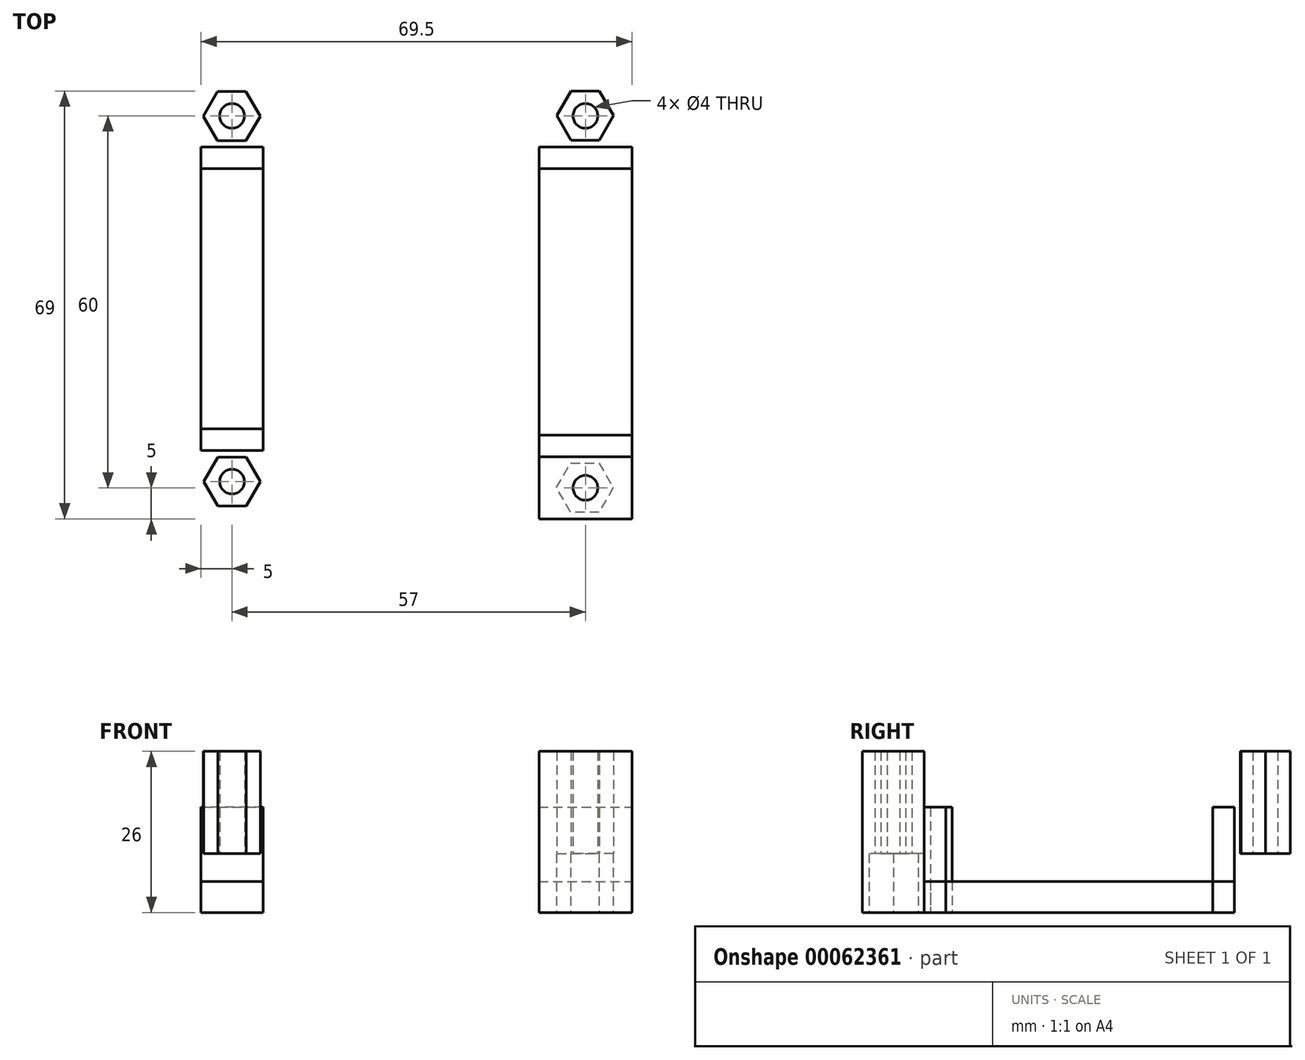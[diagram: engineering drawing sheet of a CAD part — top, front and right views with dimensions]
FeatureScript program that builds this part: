
annotation { "Feature Type Name" : "Feature", "Feature Type Description" : "" }
export const myFeature = defineFeature(function(context is Context, id is Id, definition is map)
    precondition{}
    {
        {
            var Q0;
            Q0=qCreatedBy(makeId("Top.planeOp"),FACE);
            var sketch = newSketch(context, id + "F0", { "sketchPlane" : qUnion([Q0])});
            skLineSegment(sketch, "E0.bottom", {"start": v(0, 0) * mm, "end": v(50.5, 0) * mm, "construction": true});
            skLineSegment(sketch, "E0.top", {"start": v(0, -69) * mm, "end": v(50.5, -69) * mm, "construction": true});
            skLineSegment(sketch, "E0.left", {"start": v(0, 0) * mm, "end": v(0, -69) * mm, "construction": true});
            skLineSegment(sketch, "E0.right", {"start": v(50.5, 0) * mm, "end": v(50.5, -69) * mm, "construction": true});
            skPoint(sketch, "E1", {"position": v(15, 8) * mm});
            skPoint(sketch, "E2", {"position": v(35.5, 8) * mm});
            skPoint(sketch, "E3", {"position": v(35.5, -32) * mm});
            skPoint(sketch, "E4", {"position": v(15, -32) * mm});
            skCircle(sketch, "E5", {"center": v(15, 8) * mm, "radius": 2 * mm});
            skCircle(sketch, "E6", {"center": v(35.5, 8) * mm, "radius": 2 * mm});
            skCircle(sketch, "E7", {"center": v(35.5, -32) * mm, "radius": 2 * mm});
            skCircle(sketch, "E8", {"center": v(15, -32) * mm, "radius": 2 * mm});
            skPoint(sketch, "E9", {"position": v(-9.5, 0) * mm});
            skPoint(sketch, "E10", {"position": v(60, 0) * mm});
            skPoint(sketch, "E11", {"position": v(45, 0) * mm});
            skPoint(sketch, "E12", {"position": v(0.5, 0) * mm});
            skPoint(sketch, "E13", {"position": v(60, -70) * mm});
            skPoint(sketch, "E14", {"position": v(-9.5, -69) * mm});
            skPoint(sketch, "E15", {"position": v(-9.5, -13.5) * mm});
            skPoint(sketch, "E16", {"position": v(-9.5, -55.5) * mm});
            skPoint(sketch, "E17", {"position": v(60, -13.5) * mm});
            skPoint(sketch, "E18", {"position": v(60, -56.5) * mm});
            skLineSegment(sketch, "E19.bottom", {"start": v(45, 0) * mm, "end": v(60, 0) * mm});
            skLineSegment(sketch, "E19.top", {"start": v(45, -70) * mm, "end": v(60, -70) * mm});
            skLineSegment(sketch, "E19.left", {"start": v(45, 0) * mm, "end": v(45, -70) * mm});
            skLineSegment(sketch, "E19.right", {"start": v(60, 0) * mm, "end": v(60, -70) * mm});
            skLineSegment(sketch, "E20.bottom", {"start": v(60, -13.5) * mm, "end": v(45, -13.5) * mm});
            skLineSegment(sketch, "E20.top", {"start": v(60, 0) * mm, "end": v(45, 0) * mm});
            skLineSegment(sketch, "E20.left", {"start": v(60, -13.5) * mm, "end": v(60, 0) * mm});
            skLineSegment(sketch, "E20.right", {"start": v(45, -13.5) * mm, "end": v(45, 0) * mm});
            skLineSegment(sketch, "E21.top", {"start": v(45, -56.5) * mm, "end": v(60, -56.5) * mm});
            skLineSegment(sketch, "E21.left", {"start": v(45, -70) * mm, "end": v(45, -56.5) * mm});
            skLineSegment(sketch, "E21.right", {"start": v(60, -70) * mm, "end": v(60, -56.5) * mm});
            skLineSegment(sketch, "E22.bottom", {"start": v(-9.5, -69) * mm, "end": v(0.5, -69) * mm});
            skLineSegment(sketch, "E22.top", {"start": v(-9.5, 0) * mm, "end": v(0.5, 0) * mm});
            skLineSegment(sketch, "E22.left", {"start": v(-9.5, -69) * mm, "end": v(-9.5, 0) * mm});
            skLineSegment(sketch, "E22.right", {"start": v(0.5, -69) * mm, "end": v(0.5, 0) * mm});
            skLineSegment(sketch, "E23.bottom", {"start": v(0.5, 0) * mm, "end": v(-9.5, 0) * mm});
            skLineSegment(sketch, "E23.top", {"start": v(0.5, -13.5) * mm, "end": v(-9.5, -13.5) * mm});
            skLineSegment(sketch, "E23.left", {"start": v(0.5, 0) * mm, "end": v(0.5, -13.5) * mm});
            skLineSegment(sketch, "E23.right", {"start": v(-9.5, 0) * mm, "end": v(-9.5, -13.5) * mm});
            skLineSegment(sketch, "E24.bottom", {"start": v(0.5, -69) * mm, "end": v(-9.5, -69) * mm});
            skLineSegment(sketch, "E24.top", {"start": v(0.5, -55.5) * mm, "end": v(-9.5, -55.5) * mm});
            skLineSegment(sketch, "E24.left", {"start": v(0.5, -69) * mm, "end": v(0.5, -55.5) * mm});
            skLineSegment(sketch, "E24.right", {"start": v(-9.5, -69) * mm, "end": v(-9.5, -55.5) * mm});
            skLineSegment(sketch, "E25", {"start": v(-9.5, -10) * mm, "end": v(0.5, -10) * mm});
            skLineSegment(sketch, "E26", {"start": v(-9.5, -59) * mm, "end": v(0.5, -59) * mm});
            skLineSegment(sketch, "E27", {"start": v(45, -60) * mm, "end": v(60, -60) * mm});
            skLineSegment(sketch, "E28", {"start": v(45, -10) * mm, "end": v(60, -10) * mm});
            skCircle(sketch, "E29", {"center": v(-4.5, -5) * mm, "radius": 2 * mm});
            skPoint(sketch, "E29.centerSnap0", {"position": v(-4.5, 0) * mm});
            skCircle(sketch, "E30", {"center": v(52.5, -5) * mm, "radius": 2 * mm});
            skPoint(sketch, "E30.centerSnap0", {"position": v(52.5, 0) * mm});
            skCircle(sketch, "E31", {"center": v(52.5, -65) * mm, "radius": 2 * mm});
            skPoint(sketch, "E31.centerSnap0", {"position": v(52.5, -70) * mm});
            skCircle(sketch, "E32", {"center": v(-4.5, -64) * mm, "radius": 2 * mm});
            skPoint(sketch, "E32.centerSnap0", {"position": v(-4.5, -69) * mm});
            skPoint(sketch, "E33", {"position": v(15, 16) * mm});
            skPoint(sketch, "E34", {"position": v(35.53, 16) * mm});
            skPoint(sketch, "E35", {"position": v(7, 8) * mm});
            skPoint(sketch, "E36", {"position": v(43.5, 8) * mm});
            skLineSegment(sketch, "E37", {"start": v(15, 16) * mm, "end": v(35.53, 16) * mm});
            skLineSegment(sketch, "E38", {"start": v(43.5, 8) * mm, "end": v(35.53, 16) * mm});
            skLineSegment(sketch, "E39", {"start": v(7, 8) * mm, "end": v(15, 16) * mm});
            skLineSegment(sketch, "E40", {"start": v(43.5, 8) * mm, "end": v(45, -10) * mm});
            skLineSegment(sketch, "E41", {"start": v(7, 8) * mm, "end": v(0.5, -10) * mm});
            skLineSegment(sketch, "E42", {"start": v(0.5, -59) * mm, "end": v(45, -60) * mm});
            skLineSegment(sketch, "E43", {"start": v(-58.4, 29.71) * mm, "end": v(-57.23, 30.88) * mm});
            skLineSegment(sketch, "E44", {"start": v(-57.23, 30.88) * mm, "end": v(-55.57, 30.88) * mm});
            skLineSegment(sketch, "E45", {"start": v(-55.57, 30.88) * mm, "end": v(-54.4, 29.71) * mm});
            skLineSegment(sketch, "E46", {"start": v(-54.4, 29.71) * mm, "end": v(-54.4, 28.05) * mm});
            skLineSegment(sketch, "E47", {"start": v(-54.4, 28.05) * mm, "end": v(-55.57, 26.88) * mm});
            skLineSegment(sketch, "E48", {"start": v(-55.57, 26.88) * mm, "end": v(-57.2, 26.88) * mm});
            skLineSegment(sketch, "E49", {"start": v(-57.2, 26.88) * mm, "end": v(-58.4, 28.03) * mm});
            skLineSegment(sketch, "E50", {"start": v(-58.4, 28.03) * mm, "end": v(-58.4, 29.71) * mm});
            skLineSegment(sketch, "E51.4", {"start": v(-64.18, 24.73) * mm, "end": v(-61.28, 24.73) * mm});
            skLineSegment(sketch, "E51.5", {"start": v(-61.28, 24.73) * mm, "end": v(-59.23, 22.67) * mm});
            skLineSegment(sketch, "E51.6", {"start": v(-59.23, 22.67) * mm, "end": v(-59.23, 19.78) * mm});
            skLineSegment(sketch, "E51.7", {"start": v(-59.23, 19.78) * mm, "end": v(-61.28, 17.73) * mm});
            skLineSegment(sketch, "E51.3", {"start": v(-61.28, 17.73) * mm, "end": v(-64.13, 17.73) * mm});
            skLineSegment(sketch, "E51.1", {"start": v(-64.13, 17.73) * mm, "end": v(-66.23, 19.73) * mm});
            skLineSegment(sketch, "E51.0", {"start": v(-66.23, 19.73) * mm, "end": v(-66.23, 22.67) * mm});
            skLineSegment(sketch, "E51.2", {"start": v(-66.23, 22.67) * mm, "end": v(-64.18, 24.73) * mm});
            skLineSegment(sketch, "E52.4", {"start": v(13.56, 11.51) * mm, "end": v(16.46, 11.51) * mm});
            skLineSegment(sketch, "E52.5", {"start": v(16.46, 11.51) * mm, "end": v(18.51, 9.46) * mm});
            skLineSegment(sketch, "E52.6", {"start": v(18.51, 9.46) * mm, "end": v(18.51, 6.56) * mm});
            skLineSegment(sketch, "E52.7", {"start": v(18.51, 6.56) * mm, "end": v(16.46, 4.51) * mm});
            skLineSegment(sketch, "E52.3", {"start": v(16.46, 4.51) * mm, "end": v(13.61, 4.51) * mm});
            skLineSegment(sketch, "E52.1", {"start": v(13.61, 4.51) * mm, "end": v(11.51, 6.51) * mm});
            skLineSegment(sketch, "E52.0", {"start": v(11.51, 6.51) * mm, "end": v(11.51, 9.46) * mm});
            skLineSegment(sketch, "E52.2", {"start": v(11.51, 9.46) * mm, "end": v(13.56, 11.51) * mm});
            skLineSegment(sketch, "E53.4", {"start": v(34.08, 11.49) * mm, "end": v(36.98, 11.49) * mm});
            skLineSegment(sketch, "E53.5", {"start": v(36.98, 11.49) * mm, "end": v(39.03, 9.44) * mm});
            skLineSegment(sketch, "E53.6", {"start": v(39.03, 9.44) * mm, "end": v(39.03, 6.54) * mm});
            skLineSegment(sketch, "E53.7", {"start": v(39.03, 6.54) * mm, "end": v(36.98, 4.5) * mm});
            skLineSegment(sketch, "E53.3", {"start": v(36.98, 4.5) * mm, "end": v(34.13, 4.5) * mm});
            skLineSegment(sketch, "E53.1", {"start": v(34.13, 4.5) * mm, "end": v(32.03, 6.5) * mm});
            skLineSegment(sketch, "E53.0", {"start": v(32.03, 6.5) * mm, "end": v(32.03, 9.44) * mm});
            skLineSegment(sketch, "E53.2", {"start": v(32.03, 9.44) * mm, "end": v(34.08, 11.49) * mm});
            skLineSegment(sketch, "E54.4", {"start": v(13.56, -28.5) * mm, "end": v(16.46, -28.5) * mm});
            skLineSegment(sketch, "E54.5", {"start": v(16.46, -28.5) * mm, "end": v(18.51, -30.56) * mm});
            skLineSegment(sketch, "E54.6", {"start": v(18.51, -30.56) * mm, "end": v(18.51, -33.46) * mm});
            skLineSegment(sketch, "E54.7", {"start": v(18.51, -33.46) * mm, "end": v(16.46, -35.5) * mm});
            skLineSegment(sketch, "E54.3", {"start": v(16.46, -35.5) * mm, "end": v(13.61, -35.5) * mm});
            skLineSegment(sketch, "E54.1", {"start": v(13.61, -35.5) * mm, "end": v(11.51, -33.5) * mm});
            skLineSegment(sketch, "E54.0", {"start": v(11.51, -33.5) * mm, "end": v(11.51, -30.56) * mm});
            skLineSegment(sketch, "E54.2", {"start": v(11.51, -30.56) * mm, "end": v(13.56, -28.5) * mm});
            skLineSegment(sketch, "E55.4", {"start": v(34.08, -28.54) * mm, "end": v(36.98, -28.54) * mm});
            skLineSegment(sketch, "E55.5", {"start": v(36.98, -28.54) * mm, "end": v(39.03, -30.59) * mm});
            skLineSegment(sketch, "E55.6", {"start": v(39.03, -30.59) * mm, "end": v(39.03, -33.49) * mm});
            skLineSegment(sketch, "E55.7", {"start": v(39.03, -33.49) * mm, "end": v(36.98, -35.54) * mm});
            skLineSegment(sketch, "E55.3", {"start": v(36.98, -35.54) * mm, "end": v(34.13, -35.54) * mm});
            skLineSegment(sketch, "E55.1", {"start": v(34.13, -35.54) * mm, "end": v(32.03, -33.54) * mm});
            skLineSegment(sketch, "E55.0", {"start": v(32.03, -33.54) * mm, "end": v(32.03, -30.59) * mm});
            skLineSegment(sketch, "E55.2", {"start": v(32.03, -30.59) * mm, "end": v(34.08, -28.54) * mm});
            skLineSegment(sketch, "E56.3", {"start": v(-45.37, 43.66) * mm, "end": v(-40.79, 43.66) * mm});
            skLineSegment(sketch, "E56.1", {"start": v(-40.79, 43.66) * mm, "end": v(-38.5, 39.7) * mm});
            skLineSegment(sketch, "E56.2", {"start": v(-38.5, 39.7) * mm, "end": v(-40.79, 35.74) * mm});
            skLineSegment(sketch, "E56.4", {"start": v(-40.79, 35.74) * mm, "end": v(-45.37, 35.74) * mm});
            skLineSegment(sketch, "E56.5", {"start": v(-45.37, 35.74) * mm, "end": v(-47.65, 39.7) * mm});
            skLineSegment(sketch, "E56.0", {"start": v(-47.65, 39.7) * mm, "end": v(-45.37, 43.66) * mm});
            skLineSegment(sketch, "E57.2", {"start": v(0.04, -5.04) * mm, "end": v(-2.25, -9) * mm});
            skLineSegment(sketch, "E57.1", {"start": v(-2.25, -1.08) * mm, "end": v(0.04, -5.04) * mm});
            skLineSegment(sketch, "E57.3", {"start": v(-6.82, -1.08) * mm, "end": v(-2.25, -1.08) * mm});
            skLineSegment(sketch, "E57.0", {"start": v(-9.11, -5.04) * mm, "end": v(-6.82, -1.08) * mm});
            skLineSegment(sketch, "E57.5", {"start": v(-6.82, -9) * mm, "end": v(-9.11, -5.04) * mm});
            skLineSegment(sketch, "E57.4", {"start": v(-2.25, -9) * mm, "end": v(-6.82, -9) * mm});
            skLineSegment(sketch, "E58.2", {"start": v(0.1, -64) * mm, "end": v(-2.2, -67.96) * mm});
            skLineSegment(sketch, "E58.1", {"start": v(-2.2, -60.03) * mm, "end": v(0.1, -64) * mm});
            skLineSegment(sketch, "E58.3", {"start": v(-6.77, -60.03) * mm, "end": v(-2.2, -60.03) * mm});
            skLineSegment(sketch, "E58.0", {"start": v(-9.06, -64) * mm, "end": v(-6.77, -60.03) * mm});
            skLineSegment(sketch, "E58.5", {"start": v(-6.77, -67.96) * mm, "end": v(-9.06, -64) * mm});
            skLineSegment(sketch, "E58.4", {"start": v(-2.2, -67.96) * mm, "end": v(-6.77, -67.96) * mm});
            skLineSegment(sketch, "E59.2", {"start": v(57.05, -4.96) * mm, "end": v(54.76, -8.93) * mm});
            skLineSegment(sketch, "E59.1", {"start": v(54.76, -1) * mm, "end": v(57.05, -4.96) * mm});
            skLineSegment(sketch, "E59.3", {"start": v(50.18, -1) * mm, "end": v(54.76, -1) * mm});
            skLineSegment(sketch, "E59.0", {"start": v(47.9, -4.96) * mm, "end": v(50.18, -1) * mm});
            skLineSegment(sketch, "E59.5", {"start": v(50.18, -8.93) * mm, "end": v(47.9, -4.96) * mm});
            skLineSegment(sketch, "E59.4", {"start": v(54.76, -8.93) * mm, "end": v(50.18, -8.93) * mm});
            skLineSegment(sketch, "E60.2", {"start": v(57, -64.96) * mm, "end": v(54.7, -68.92) * mm});
            skLineSegment(sketch, "E60.1", {"start": v(54.7, -61) * mm, "end": v(57, -64.96) * mm});
            skLineSegment(sketch, "E60.3", {"start": v(50.12, -61) * mm, "end": v(54.7, -61) * mm});
            skLineSegment(sketch, "E60.0", {"start": v(47.84, -64.96) * mm, "end": v(50.12, -61) * mm});
            skLineSegment(sketch, "E60.5", {"start": v(50.12, -68.92) * mm, "end": v(47.84, -64.96) * mm});
            skLineSegment(sketch, "E60.4", {"start": v(54.7, -68.92) * mm, "end": v(50.12, -68.92) * mm});
            skSolve(sketch);
        }
        {
            var Q0;
            Q0=makeQuery(id+"F0.imprint","IMPRINT",FACE,{"disambiguationData":[TD([[makeQuery(id+"F0.imprint","IMPRINT",EDGE,{"derivedFrom":sQuery(id+"F0.wireOp",EDGE,"E19.left")}),1.0]])]});
            var Q1;
            Q1=makeQuery(id+"F0.imprint","IMPRINT",FACE,{"disambiguationData":[TD([[makeQuery(id+"F0.imprint","IMPRINT",EDGE,{"derivedFrom":sQuery(id+"F0.wireOp",EDGE,"E22.left")}),-1.0]])]});
            extrude(context, id + "F1", {"entities" : qUnion([Q0, Q1]), "depth" : 5 * mm});
        }
        {
            var Q0;
            {var subQ0=sQuery(id+"F0.wireOp",EDGE,"E24.top");Q0=makeQuery(id+"F0.imprint","IMPRINT",FACE,{"disambiguationData":[TD([[makeQuery(id+"F0.imprint","IMPRINT",EDGE,{"derivedFrom":subQ0}),1.0]])]});}
            var Q1;
            {var subQ0=sQuery(id+"F0.wireOp",EDGE,"E23.top");Q1=makeQuery(id+"F0.imprint","IMPRINT",FACE,{"disambiguationData":[TD([[makeQuery(id+"F0.imprint","IMPRINT",EDGE,{"derivedFrom":subQ0}),-1.0]])]});}
            var Q2;
            {var subQ0=sQuery(id+"F0.wireOp",EDGE,"E20.bottom");Q2=makeQuery(id+"F0.imprint","IMPRINT",FACE,{"disambiguationData":[TD([[makeQuery(id+"F0.imprint","IMPRINT",EDGE,{"derivedFrom":subQ0}),-1.0]])]});}
            var Q3;
            {var subQ0=sQuery(id+"F0.wireOp",EDGE,"E21.top");Q3=makeQuery(id+"F0.imprint","IMPRINT",FACE,{"disambiguationData":[TD([[makeQuery(id+"F0.imprint","IMPRINT",EDGE,{"derivedFrom":subQ0}),-1.0]])]});}
            extrude(context, id + "F2", {"entities" : qUnion([Q0, Q1, Q2, Q3]), "depth" : 17 * mm});
        }
        {
            var Q0;
            {var subQ1=sQuery(id+"F0.wireOp",EDGE,"E19.top");Q0=makeQuery(id+"F0.imprint","IMPRINT",FACE,{"disambiguationData":[TD([[makeQuery(id+"F0.imprint","IMPRINT",EDGE,{"derivedFrom":subQ1}),1.0]])]});}
            var Q1;
            Q1=makeQuery(id+"F0.imprint","IMPRINT",FACE,{"disambiguationData":[TD([[makeQuery(id+"F0.imprint","IMPRINT",EDGE,{"derivedFrom":sQuery(id+"F0.wireOp",EDGE,"E31")}),-1.0]])]});
            var Q2;
            {var subQ0=sQuery(id+"F0.wireOp",EDGE,"E24.bottom");Q2=makeQuery(id+"F0.imprint","IMPRINT",FACE,{"disambiguationData":[TD([[makeQuery(id+"F0.imprint","IMPRINT",EDGE,{"derivedFrom":subQ0}),-1.0]])]});}
            var Q3;
            Q3=makeQuery(id+"F0.imprint","IMPRINT",FACE,{"disambiguationData":[TD([[makeQuery(id+"F0.imprint","IMPRINT",EDGE,{"derivedFrom":sQuery(id+"F0.wireOp",EDGE,"E32")}),-1.0]])]});
            var Q4;
            Q4=makeQuery(id+"F0.imprint","IMPRINT",FACE,{"disambiguationData":[TD([[makeQuery(id+"F0.imprint","IMPRINT",EDGE,{"derivedFrom":sQuery(id+"F0.wireOp",EDGE,"E29")}),-1.0]])]});
            var Q5;
            {var subQ1=sQuery(id+"F0.wireOp",EDGE,"E23.bottom");Q5=makeQuery(id+"F0.imprint","IMPRINT",FACE,{"disambiguationData":[TD([[makeQuery(id+"F0.imprint","IMPRINT",EDGE,{"derivedFrom":subQ1}),1.0]])]});}
            var Q6;
            Q6=makeQuery(id+"F0.imprint","IMPRINT",FACE,{"disambiguationData":[TD([[makeQuery(id+"F0.imprint","IMPRINT",EDGE,{"derivedFrom":sQuery(id+"F0.wireOp",EDGE,"E30")}),-1.0]])]});
            var Q7;
            {var subQ1=sQuery(id+"F0.wireOp",EDGE,"E20.top");Q7=makeQuery(id+"F0.imprint","IMPRINT",FACE,{"disambiguationData":[TD([[makeQuery(id+"F0.imprint","IMPRINT",EDGE,{"derivedFrom":subQ1}),1.0]])]});}
            extrude(context, id + "F3", {"entities" : qUnion([Q0, Q1, Q2, Q3, Q4, Q5, Q6, Q7]), "depth" : 26 * mm});
        }
        {
            var Q0;
            Q0=makeQuery(id+"F0.imprint","IMPRINT",FACE,{"disambiguationData":[TD([[makeQuery(id+"F0.imprint","IMPRINT",EDGE,{"derivedFrom":sQuery(id+"F0.wireOp",EDGE,"E31")}),-1.0]])]});
            var Q1;
            Q1=makeQuery(id+"F0.imprint","IMPRINT",FACE,{"disambiguationData":[TD([[makeQuery(id+"F0.imprint","IMPRINT",EDGE,{"derivedFrom":sQuery(id+"F0.wireOp",EDGE,"E30")}),-1.0]])]});
            var Q2;
            Q2=makeQuery(id+"F0.imprint","IMPRINT",FACE,{"disambiguationData":[TD([[makeQuery(id+"F0.imprint","IMPRINT",EDGE,{"derivedFrom":sQuery(id+"F0.wireOp",EDGE,"E32")}),-1.0]])]});
            var Q3;
            Q3=makeQuery(id+"F0.imprint","IMPRINT",FACE,{"disambiguationData":[TD([[makeQuery(id+"F0.imprint","IMPRINT",EDGE,{"derivedFrom":sQuery(id+"F0.wireOp",EDGE,"E29")}),-1.0]])]});
            extrude(context, id + "F4", {"entities" : qUnion([Q0, Q1, Q2, Q3]), "operationType" : NewBodyOperationType.REMOVE, "depth" : 9.5 * mm});
        }
    });
